# Revit family: 1
name_source: partatom
category: Generic Models
revit_build: Autodesk Revit 2018 (Build: 20190510_1515(x64)
units: mm (PartAtom-declared; Revit-internal decimal feet)

## family parameters
Can host rebar = No
Cut with Voids When Loaded = No
Host = Face
OmniClass Number = 23.31.25.25
OmniClass Title = Towel Bars
Part Type = Normal
Room Calculation Point = No
Round Connector Dimension = Use Diameter
Shared = No

## types (1)
- Karree Towel rail 70x668x35 mm - 009959
    BIMobject category = Bathroom Accessories
    Default Elevation = 1219 mm
    Description = Duravit Karree Towel rail Chrome 70x668x35 mm - 0099591000
    Design country = Germany
    ETIM classification = EC010551 | Towel holder
    Edition number = 1
    IFC Classification = Furnishing Element
    Installation instructions = https://pro.duravit.com
    Main material = Duravit - Metal - 10 - Chrome
    Manufacturer = Duravit
    Manufacturer country = Germany
    Manufacturer name = DURAVIT AG
    Masterformat 2014 Code = 10 28 00
    Masterformat 2014 Description = Toilet, Bath, and Laundry Accessories
    Material main = Brass
    Model = Karree Towel rail 70x668x35 mm - 009959
    OmniClass Code = 23-31 25 25
    OmniClass Description = Towel Bars
    Product Guid = 56bbd802-6539-4465-aa07-53833b63f80c
    Product SKU = Karree-Towel-rail-70x668x35-mm-009959
    Product certification = https://pro.duravit.com
    Product data url = https://bimobject.com
    Product family = Karree
    Product group = Towel rail
    Product name = Karree Towel rail 70x668x35 mm - 009959
    Product url = https://pro.duravit.com
    QR code = https://bimobject.com
    Technical description = https://pro.duravit.com
    UNSPSC Code = 301815
    URL = https://www.duravit.com
    Uniclass 2015 Code = Pr_40_20_76_90
    Uniclass 2015 Name = Towel rails
    Uniformat II Code = E2010
    Uniformat II Description = Fixed Furnishings
    Weight Net (Kg) = 0.7
    Youtube clip = https://pro.duravit.com

## geometry (parser evidence)
native form markers: Sweep x4
no freeform markers — native parametric forms only
